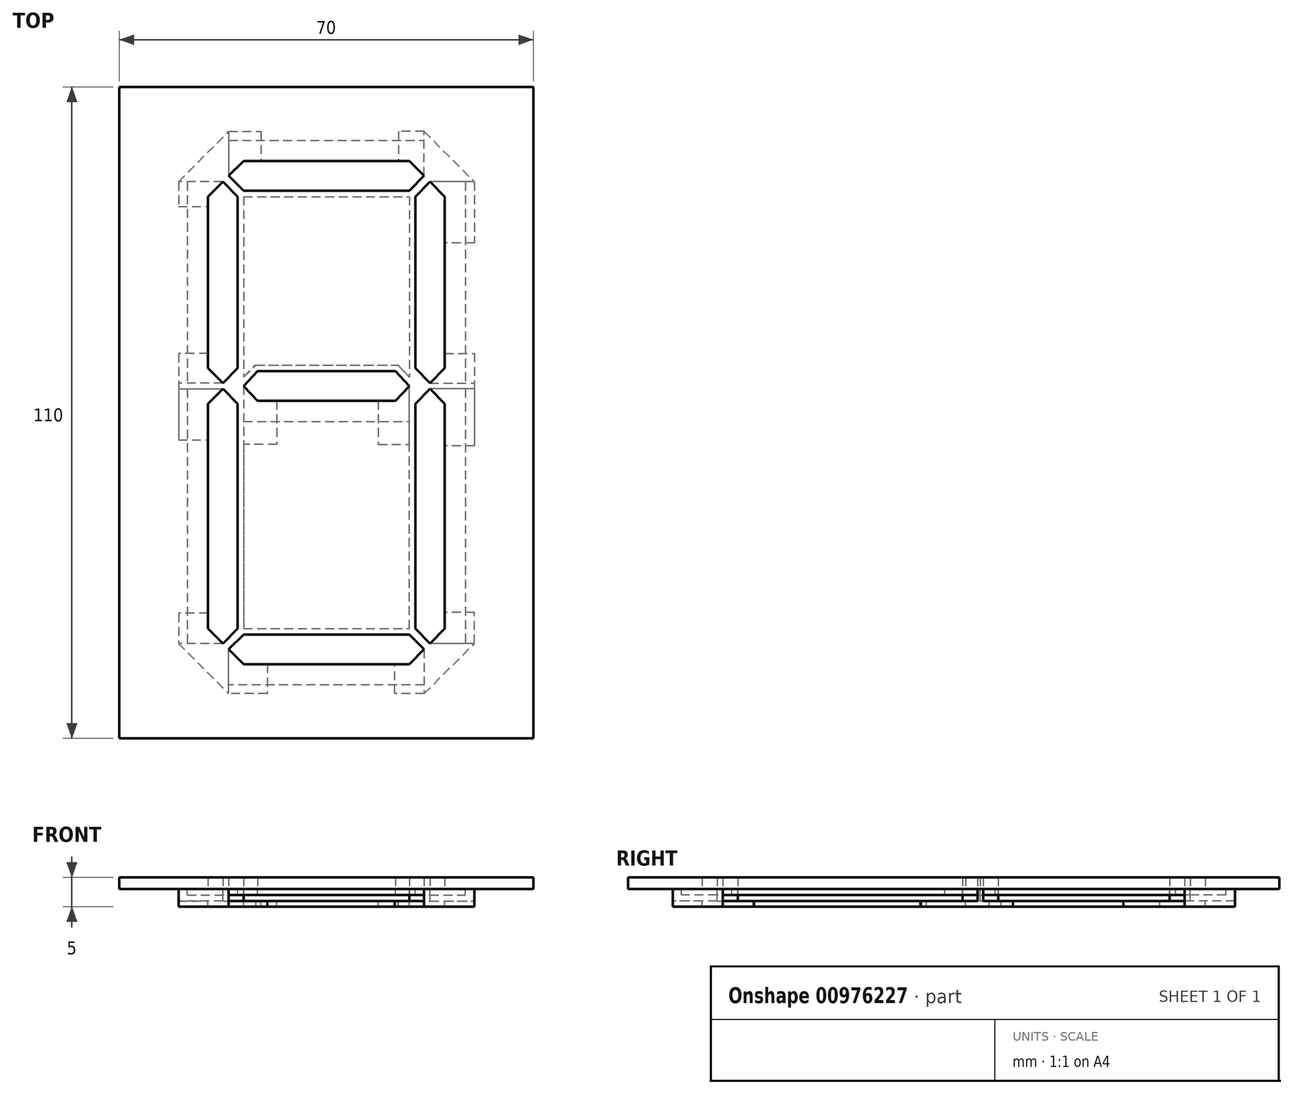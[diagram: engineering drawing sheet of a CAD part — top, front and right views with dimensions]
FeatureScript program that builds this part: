
annotation { "Feature Type Name" : "Feature", "Feature Type Description" : "" }
export const myFeature = defineFeature(function(context is Context, id is Id, definition is map)
    precondition{}
    {
        {
            var Q0;
            Q0=qCreatedBy(makeId("Top.planeOp"),FACE);
            var sketch = newSketch(context, id + "F0", { "sketchPlane" : qUnion([Q0])});
            skLineSegment(sketch, "E0.bottom", {"start": v(0, 0) * mm, "end": v(70, 0) * mm});
            skLineSegment(sketch, "E0.top", {"start": v(0, 110) * mm, "end": v(70, 110) * mm});
            skLineSegment(sketch, "E0.left", {"start": v(0, 0) * mm, "end": v(0, 110) * mm});
            skLineSegment(sketch, "E0.right", {"start": v(70, 0) * mm, "end": v(70, 110) * mm});
            skLineSegment(sketch, "E1.bottom", {"start": v(17.5, 95) * mm, "end": v(52.5, 95) * mm, "construction": true});
            skLineSegment(sketch, "E1.top", {"start": v(17.5, 15) * mm, "end": v(52.5, 15) * mm, "construction": true});
            skLineSegment(sketch, "E1.left", {"start": v(17.5, 95) * mm, "end": v(17.5, 15) * mm, "construction": true});
            skLineSegment(sketch, "E1.right", {"start": v(52.5, 95) * mm, "end": v(52.5, 15) * mm, "construction": true});
            skLineSegment(sketch, "E2", {"start": v(18.5, 95) * mm, "end": v(21, 97.5) * mm});
            skLineSegment(sketch, "E3", {"start": v(21, 97.5) * mm, "end": v(49, 97.5) * mm});
            skLineSegment(sketch, "E4", {"start": v(49, 97.5) * mm, "end": v(51.5, 95) * mm});
            skLineSegment(sketch, "E5.MirrorCS", {"start": v(18.5, 95) * mm, "end": v(21, 92.5) * mm});
            skLineSegment(sketch, "E6.MirrorCS", {"start": v(21, 92.5) * mm, "end": v(49, 92.5) * mm});
            skLineSegment(sketch, "E7.MirrorCS", {"start": v(49, 92.5) * mm, "end": v(51.5, 95) * mm});
            skLineSegment(sketch, "E8", {"start": v(17.5, 95) * mm, "end": v(36.4, 76.1) * mm, "construction": true});
            skLineSegment(sketch, "E9", {"start": v(17.5, 94) * mm, "end": v(20, 91.5) * mm});
            skLineSegment(sketch, "E10", {"start": v(20, 91.5) * mm, "end": v(20, 62.5) * mm});
            skLineSegment(sketch, "E11", {"start": v(20, 62.5) * mm, "end": v(17.5, 60) * mm});
            skLineSegment(sketch, "E12.MirrorCS", {"start": v(17.5, 94) * mm, "end": v(15, 91.5) * mm});
            skLineSegment(sketch, "E13.MirrorCS", {"start": v(15, 91.5) * mm, "end": v(15, 62.5) * mm});
            skLineSegment(sketch, "E14.MirrorCS", {"start": v(15, 62.5) * mm, "end": v(17.5, 60) * mm});
            skLineSegment(sketch, "E15.MirrorCS", {"start": v(21, 17.5) * mm, "end": v(49, 17.5) * mm});
            skLineSegment(sketch, "E16.MirrorCS", {"start": v(49, 17.5) * mm, "end": v(51.5, 15) * mm});
            skLineSegment(sketch, "E17.MirrorCS", {"start": v(49, 12.5) * mm, "end": v(51.5, 15) * mm});
            skLineSegment(sketch, "E18.MirrorCS", {"start": v(21, 12.5) * mm, "end": v(49, 12.5) * mm});
            skLineSegment(sketch, "E19.MirrorCS", {"start": v(18.5, 15) * mm, "end": v(21, 12.5) * mm});
            skLineSegment(sketch, "E20.MirrorCS", {"start": v(18.5, 15) * mm, "end": v(21, 17.5) * mm});
            skLineSegment(sketch, "E21.MirrorCS", {"start": v(17.5, 16) * mm, "end": v(20, 18.5) * mm});
            skLineSegment(sketch, "E22.MirrorCS", {"start": v(17.5, 16) * mm, "end": v(15, 18.5) * mm});
            skLineSegment(sketch, "E23.MirrorCS", {"start": v(15, 18.5) * mm, "end": v(15, 56.5) * mm});
            skLineSegment(sketch, "E24.MirrorCS", {"start": v(20, 18.5) * mm, "end": v(20, 56.5) * mm});
            skLineSegment(sketch, "E25.MirrorCS", {"start": v(20, 56.5) * mm, "end": v(17.5, 59) * mm});
            skLineSegment(sketch, "E26.MirrorCS", {"start": v(15, 56.5) * mm, "end": v(17.5, 59) * mm});
            skLineSegment(sketch, "E27", {"start": v(35, 92.07) * mm, "end": v(35, 15) * mm, "construction": true});
            skLineSegment(sketch, "E28.MirrorCS", {"start": v(52.5, 94) * mm, "end": v(50, 91.5) * mm});
            skLineSegment(sketch, "E29.MirrorCS", {"start": v(52.5, 94) * mm, "end": v(55, 91.5) * mm});
            skLineSegment(sketch, "E30.MirrorCS", {"start": v(55, 91.5) * mm, "end": v(55, 62.5) * mm});
            skLineSegment(sketch, "E31.MirrorCS", {"start": v(50, 91.5) * mm, "end": v(50, 62.5) * mm});
            skLineSegment(sketch, "E32.MirrorCS", {"start": v(50, 62.5) * mm, "end": v(52.5, 60) * mm});
            skLineSegment(sketch, "E33.MirrorCS", {"start": v(55, 62.5) * mm, "end": v(52.5, 60) * mm});
            skLineSegment(sketch, "E34.MirrorCS", {"start": v(50, 56.5) * mm, "end": v(52.5, 59) * mm});
            skLineSegment(sketch, "E35.MirrorCS", {"start": v(55, 56.5) * mm, "end": v(52.5, 59) * mm});
            skLineSegment(sketch, "E36.MirrorCS", {"start": v(55, 18.5) * mm, "end": v(55, 56.5) * mm});
            skLineSegment(sketch, "E37.MirrorCS", {"start": v(50, 18.5) * mm, "end": v(50, 56.5) * mm});
            skLineSegment(sketch, "E38.MirrorCS", {"start": v(52.5, 16) * mm, "end": v(50, 18.5) * mm});
            skLineSegment(sketch, "E39.MirrorCS", {"start": v(52.5, 16) * mm, "end": v(55, 18.5) * mm});
            skLineSegment(sketch, "E40", {"start": v(21, 59.5) * mm, "end": v(23.33, 62) * mm});
            skLineSegment(sketch, "E41", {"start": v(23.33, 62) * mm, "end": v(46.67, 62) * mm});
            skLineSegment(sketch, "E42", {"start": v(46.67, 62) * mm, "end": v(49, 59.5) * mm});
            skLineSegment(sketch, "E43.MirrorCS", {"start": v(21, 59.5) * mm, "end": v(23.33, 57) * mm});
            skLineSegment(sketch, "E44.MirrorCS", {"start": v(23.33, 57) * mm, "end": v(46.67, 57) * mm});
            skLineSegment(sketch, "E45.MirrorCS", {"start": v(46.67, 57) * mm, "end": v(49, 59.5) * mm});
            skLineSegment(sketch, "E46", {"start": v(52.5, 59.5) * mm, "end": v(15.97, 59.5) * mm, "construction": true});
            skLineSegment(sketch, "E47", {"start": v(52.5, 59) * mm, "end": v(52.5, 60) * mm, "construction": true});
            skSolve(sketch);
        }
        {
            var Q0;
            Q0 = qSketchRegion(id + "F0", true);
            extrude(context, id + "F1", {"entities" : qUnion([Q0]), "depth" : 2 * mm, "offsetDistance" : 25 * mm});
        }
        {
            var Q0;
            Q0=makeQuery(id+"F1.opExtrude","CAP_FACE",FACE,{"disambiguationData":[OSD([sQuery(id+"F0.wireOp",EDGE,"E0.bottom"),sQuery(id+"F0.wireOp",EDGE,"E0.top"),sQuery(id+"F0.wireOp",EDGE,"E0.left"),sQuery(id+"F0.wireOp",EDGE,"E0.right"),sQuery(id+"F0.wireOp",EDGE,"E2"),sQuery(id+"F0.wireOp",EDGE,"E3"),sQuery(id+"F0.wireOp",EDGE,"E4"),sQuery(id+"F0.wireOp",EDGE,"E5.MirrorCS"),sQuery(id+"F0.wireOp",EDGE,"E6.MirrorCS"),sQuery(id+"F0.wireOp",EDGE,"E7.MirrorCS"),sQuery(id+"F0.wireOp",EDGE,"E9"),sQuery(id+"F0.wireOp",EDGE,"E10"),sQuery(id+"F0.wireOp",EDGE,"E11"),sQuery(id+"F0.wireOp",EDGE,"E12.MirrorCS"),sQuery(id+"F0.wireOp",EDGE,"E13.MirrorCS"),sQuery(id+"F0.wireOp",EDGE,"E14.MirrorCS"),sQuery(id+"F0.wireOp",EDGE,"E15.MirrorCS"),sQuery(id+"F0.wireOp",EDGE,"E16.MirrorCS"),sQuery(id+"F0.wireOp",EDGE,"E17.MirrorCS"),sQuery(id+"F0.wireOp",EDGE,"E18.MirrorCS"),sQuery(id+"F0.wireOp",EDGE,"E19.MirrorCS"),sQuery(id+"F0.wireOp",EDGE,"E20.MirrorCS"),sQuery(id+"F0.wireOp",EDGE,"E21.MirrorCS"),sQuery(id+"F0.wireOp",EDGE,"E22.MirrorCS"),sQuery(id+"F0.wireOp",EDGE,"E23.MirrorCS"),sQuery(id+"F0.wireOp",EDGE,"E24.MirrorCS"),sQuery(id+"F0.wireOp",EDGE,"E25.MirrorCS"),sQuery(id+"F0.wireOp",EDGE,"E26.MirrorCS"),sQuery(id+"F0.wireOp",EDGE,"E28.MirrorCS"),sQuery(id+"F0.wireOp",EDGE,"E29.MirrorCS"),sQuery(id+"F0.wireOp",EDGE,"E30.MirrorCS"),sQuery(id+"F0.wireOp",EDGE,"E31.MirrorCS"),sQuery(id+"F0.wireOp",EDGE,"E32.MirrorCS"),sQuery(id+"F0.wireOp",EDGE,"E33.MirrorCS"),sQuery(id+"F0.wireOp",EDGE,"E34.MirrorCS"),sQuery(id+"F0.wireOp",EDGE,"E35.MirrorCS"),sQuery(id+"F0.wireOp",EDGE,"E36.MirrorCS"),sQuery(id+"F0.wireOp",EDGE,"E37.MirrorCS"),sQuery(id+"F0.wireOp",EDGE,"E38.MirrorCS"),sQuery(id+"F0.wireOp",EDGE,"E39.MirrorCS"),sQuery(id+"F0.wireOp",EDGE,"E40"),sQuery(id+"F0.wireOp",EDGE,"E41"),sQuery(id+"F0.wireOp",EDGE,"E42"),sQuery(id+"F0.wireOp",EDGE,"E43.MirrorCS"),sQuery(id+"F0.wireOp",EDGE,"E44.MirrorCS"),sQuery(id+"F0.wireOp",EDGE,"E45.MirrorCS")])],"isStart":true});
            var sketch = newSketch(context, id + "F2", { "sketchPlane" : qUnion([Q0])});
            skLineSegment(sketch, "E48.0", {"start": v(49, -17.5) * mm, "end": v(51.5, -15) * mm});
            skLineSegment(sketch, "E49.0", {"start": v(52.5, -16) * mm, "end": v(50, -18.5) * mm});
            skLineSegment(sketch, "E50.0", {"start": v(50, -18.5) * mm, "end": v(50, -56.5) * mm});
            skLineSegment(sketch, "E51.0", {"start": v(21, -17.5) * mm, "end": v(49, -17.5) * mm});
            skLineSegment(sketch, "E52.0", {"start": v(18.5, -15) * mm, "end": v(21, -17.5) * mm});
            skLineSegment(sketch, "E53.0", {"start": v(17.5, -16) * mm, "end": v(20, -18.5) * mm});
            skLineSegment(sketch, "E54.0", {"start": v(20, -18.5) * mm, "end": v(20, -56.5) * mm});
            skLineSegment(sketch, "E55.0", {"start": v(20, -56.5) * mm, "end": v(17.5, -59) * mm});
            skLineSegment(sketch, "E56.0", {"start": v(50, -56.5) * mm, "end": v(52.5, -59) * mm});
            skLineSegment(sketch, "E57.0", {"start": v(50, -62.5) * mm, "end": v(52.5, -60) * mm});
            skLineSegment(sketch, "E58.0", {"start": v(50, -91.5) * mm, "end": v(50, -62.5) * mm});
            skLineSegment(sketch, "E59.0", {"start": v(20, -62.5) * mm, "end": v(17.5, -60) * mm});
            skLineSegment(sketch, "E60.0", {"start": v(20, -91.5) * mm, "end": v(20, -62.5) * mm});
            skLineSegment(sketch, "E61.0", {"start": v(17.5, -94) * mm, "end": v(20, -91.5) * mm});
            skLineSegment(sketch, "E62.0", {"start": v(21, -92.5) * mm, "end": v(49, -92.5) * mm});
            skLineSegment(sketch, "E63.0", {"start": v(18.5, -95) * mm, "end": v(21, -92.5) * mm});
            skLineSegment(sketch, "E64.0", {"start": v(52.5, -94) * mm, "end": v(50, -91.5) * mm});
            skLineSegment(sketch, "E65.0", {"start": v(49, -92.5) * mm, "end": v(51.5, -95) * mm});
            skLineSegment(sketch, "E66.0", {"start": v(49, -91.5) * mm, "end": v(49, -61.03) * mm});
            skLineSegment(sketch, "E67.0", {"start": v(21, -91.5) * mm, "end": v(49, -91.5) * mm});
            skLineSegment(sketch, "E68.0", {"start": v(21, -91.5) * mm, "end": v(21, -60.97) * mm});
            skLineSegment(sketch, "E69.0", {"start": v(49, -18.5) * mm, "end": v(49, -51.91) * mm});
            skLineSegment(sketch, "E70.0", {"start": v(21, -18.5) * mm, "end": v(49, -18.5) * mm});
            skLineSegment(sketch, "E71.0", {"start": v(21, -18.5) * mm, "end": v(21, -51.91) * mm});
            skLineSegment(sketch, "E72.0", {"start": v(46.67, -62) * mm, "end": v(49, -59.5) * mm});
            skLineSegment(sketch, "E73.0", {"start": v(23.33, -62) * mm, "end": v(46.67, -62) * mm});
            skLineSegment(sketch, "E74.0", {"start": v(21, -59.5) * mm, "end": v(23.33, -62) * mm});
            skLineSegment(sketch, "E75.0", {"start": v(47.1, -63) * mm, "end": v(48.94, -61.03) * mm});
            skLineSegment(sketch, "E75.1", {"start": v(22.9, -63) * mm, "end": v(47.1, -63) * mm});
            skLineSegment(sketch, "E75.2", {"start": v(21, -60.97) * mm, "end": v(22.9, -63) * mm});
            skLineSegment(sketch, "E76", {"start": v(52.5, -60) * mm, "end": v(60, -60) * mm});
            skLineSegment(sketch, "E77", {"start": v(60, -60) * mm, "end": v(60, -59) * mm});
            skLineSegment(sketch, "E78", {"start": v(60, -59) * mm, "end": v(52.5, -59) * mm});
            skLineSegment(sketch, "E79", {"start": v(17.5, -60) * mm, "end": v(10, -60) * mm});
            skLineSegment(sketch, "E80", {"start": v(10, -60) * mm, "end": v(10, -59) * mm});
            skLineSegment(sketch, "E81", {"start": v(10, -59) * mm, "end": v(17.5, -59) * mm});
            skLineSegment(sketch, "E82", {"start": v(17.5, -94) * mm, "end": v(10, -94) * mm});
            skLineSegment(sketch, "E83", {"start": v(10, -94) * mm, "end": v(18.5, -102.5) * mm});
            skLineSegment(sketch, "E84", {"start": v(18.5, -102.5) * mm, "end": v(18.5, -95) * mm});
            skLineSegment(sketch, "E85", {"start": v(51.5, -95) * mm, "end": v(51.5, -102.5) * mm});
            skLineSegment(sketch, "E86", {"start": v(51.5, -102.5) * mm, "end": v(60, -94) * mm});
            skLineSegment(sketch, "E87", {"start": v(60, -94) * mm, "end": v(52.5, -94) * mm});
            skLineSegment(sketch, "E88", {"start": v(17.5, -16) * mm, "end": v(10, -16) * mm});
            skLineSegment(sketch, "E89", {"start": v(10, -16) * mm, "end": v(18.5, -7.5) * mm});
            skLineSegment(sketch, "E90", {"start": v(18.5, -7.5) * mm, "end": v(18.5, -15) * mm});
            skLineSegment(sketch, "E91", {"start": v(51.5, -15) * mm, "end": v(51.5, -7.5) * mm});
            skLineSegment(sketch, "E92", {"start": v(51.5, -7.5) * mm, "end": v(60, -16) * mm});
            skLineSegment(sketch, "E93", {"start": v(60, -16) * mm, "end": v(52.5, -16) * mm});
            skLineSegment(sketch, "E94", {"start": v(21, -59.5) * mm, "end": v(21, -51.91) * mm});
            skPoint(sketch, "E95.end.orphan", {"position": v(13.46, -52.9) * mm});
            skPoint(sketch, "E95.start.orphan", {"position": v(13.46, -51.84) * mm});
            skLineSegment(sketch, "E96", {"start": v(49, -61.03) * mm, "end": v(48.94, -61.03) * mm});
            skLineSegment(sketch, "E97", {"start": v(49, -59.5) * mm, "end": v(49, -51.91) * mm});
            skSolve(sketch);
        }
        {
            var Q0;
            Q0 = qSketchRegion(id + "F2", true);
            var Q1;
            Q1=makeQuery(id+"F2.imprint","IMPRINT",FACE,{"disambiguationData":[TD([[makeQuery(id+"F2.imprint","IMPRINT",EDGE,{"derivedFrom":sQuery(id+"F2.wireOp",EDGE,"E72.0")}),-1.0]])]});
            extrude(context, id + "F3", {"entities" : qUnion([Q0, Q1]), "operationType" : NewBodyOperationType.ADD, "depth" : 2 * mm, "offsetDistance" : 25 * mm});
        }
        {
            var Q0;
            Q0=makeQuery(id+"F3.opExtrude","CAP_FACE",FACE,{"disambiguationData":[OSD([sQuery(id+"F2.wireOp",EDGE,"E48.0"),sQuery(id+"F2.wireOp",EDGE,"E49.0"),sQuery(id+"F2.wireOp",EDGE,"E50.0"),sQuery(id+"F2.wireOp",EDGE,"E51.0"),sQuery(id+"F2.wireOp",EDGE,"E52.0"),sQuery(id+"F2.wireOp",EDGE,"E53.0"),sQuery(id+"F2.wireOp",EDGE,"E54.0"),sQuery(id+"F2.wireOp",EDGE,"E55.0"),sQuery(id+"F2.wireOp",EDGE,"E56.0"),sQuery(id+"F2.wireOp",EDGE,"E57.0"),sQuery(id+"F2.wireOp",EDGE,"E58.0"),sQuery(id+"F2.wireOp",EDGE,"E59.0"),sQuery(id+"F2.wireOp",EDGE,"E60.0"),sQuery(id+"F2.wireOp",EDGE,"E61.0"),sQuery(id+"F2.wireOp",EDGE,"E62.0"),sQuery(id+"F2.wireOp",EDGE,"E63.0"),sQuery(id+"F2.wireOp",EDGE,"E64.0"),sQuery(id+"F2.wireOp",EDGE,"E65.0"),sQuery(id+"F2.wireOp",EDGE,"E66.0"),sQuery(id+"F2.wireOp",EDGE,"E67.0"),sQuery(id+"F2.wireOp",EDGE,"E68.0"),sQuery(id+"F2.wireOp",EDGE,"E69.0"),sQuery(id+"F2.wireOp",EDGE,"E70.0"),sQuery(id+"F2.wireOp",EDGE,"E71.0"),sQuery(id+"F2.wireOp",EDGE,"84MnlcbP-1qpu-Rj2J-FLr8-rwROh0f0MHm2"),sQuery(id+"F2.wireOp",EDGE,"LZrshJra-HxY4-wUjW-u9oj-DeEecagEfHDl"),sQuery(id+"F2.wireOp",EDGE,"1782aa05-fe14-407d-a0ca-22a35b96d353.0"),sQuery(id+"F2.wireOp",EDGE,"6b285926-bf98-404c-bd19-462a9478543c.0"),sQuery(id+"F2.wireOp",EDGE,"d8a9666b-d601-445d-a0cd-ca6338d9dcee.0"),sQuery(id+"F2.wireOp",EDGE,"e9a28232-7184-4cf5-acbe-2da583ff58bf.0"),sQuery(id+"F2.wireOp",EDGE,"kZ9Jm4wK-r8F3-Mryh-ujSV-tKrf8OWitTA8"),sQuery(id+"F2.wireOp",EDGE,"QViILa1C-kdha-76VF-oS10-NTMmApzbaOET"),sQuery(id+"F2.wireOp",EDGE,"p2RoQ5Td-hEyZ-tQ5M-2kDP-IsppDfMx4xtr"),sQuery(id+"F2.wireOp",EDGE,"9UdBR3Zx-Fciw-YJRm-m8R1-SlRN9uOtdQAB")])],"isStart":false});
            var sketch = newSketch(context, id + "F4", { "sketchPlane" : qUnion([Q0])});
            skLineSegment(sketch, "E98.0", {"start": v(44.1, -91.5) * mm, "end": v(49, -91.5) * mm});
            skLineSegment(sketch, "E99.0", {"start": v(21, -91.5) * mm, "end": v(44.1, -91.5) * mm});
            skLineSegment(sketch, "E100.0", {"start": v(21, -60.97) * mm, "end": v(21, -91.5) * mm});
            skLineSegment(sketch, "E101.0", {"start": v(21, -68.96) * mm, "end": v(21, -60.97) * mm});
            skLineSegment(sketch, "E102.0", {"start": v(21, -18.5) * mm, "end": v(21, -49.63) * mm});
            skLineSegment(sketch, "E103.0", {"start": v(21, -18.5) * mm, "end": v(49, -18.5) * mm});
            skLineSegment(sketch, "E104.0", {"start": v(49, -18.5) * mm, "end": v(49, -18.5) * mm});
            skLineSegment(sketch, "E105.0", {"start": v(49, -18.5) * mm, "end": v(49, -49.63) * mm});
            skLineSegment(sketch, "E106.0", {"start": v(49, -91.5) * mm, "end": v(49, -61.03) * mm});
            skLineSegment(sketch, "E107.0", {"start": v(23.92, -97.5) * mm, "end": v(47.2, -97.5) * mm});
            skLineSegment(sketch, "E108.0", {"start": v(15, -89.86) * mm, "end": v(15, -65) * mm});
            skLineSegment(sketch, "E109.0", {"start": v(15, -21.1) * mm, "end": v(15, -50.37) * mm});
            skLineSegment(sketch, "E110.0", {"start": v(25, -12.5) * mm, "end": v(46.54, -12.5) * mm});
            skLineSegment(sketch, "E111.0", {"start": v(55, -21.25) * mm, "end": v(55, -49.39) * mm});
            skLineSegment(sketch, "E112.0", {"start": v(55, -83.67) * mm, "end": v(55, -65.02) * mm});
            skLineSegment(sketch, "E113.0", {"start": v(23.1, -63) * mm, "end": v(47.1, -63) * mm});
            skLineSegment(sketch, "E114.0", {"start": v(21, -60.97) * mm, "end": v(23.1, -63) * mm});
            skLineSegment(sketch, "E115.0", {"start": v(26.62, -57) * mm, "end": v(43.76, -57) * mm});
            skLineSegment(sketch, "E116.0", {"start": v(49, -61.03) * mm, "end": v(47.1, -63) * mm});
            skLineSegment(sketch, "E117.trimOffspring", {"start": v(21, -60.97) * mm, "end": v(21, -68.96) * mm});
            skPoint(sketch, "E118.orphan", {"position": v(21, -55.59) * mm});
            skLineSegment(sketch, "E119.0", {"start": v(10, -94) * mm, "end": v(18.5, -102.5) * mm});
            skLineSegment(sketch, "E120.0", {"start": v(51.5, -102.5) * mm, "end": v(60, -94) * mm});
            skLineSegment(sketch, "E121", {"start": v(51.5, -102.5) * mm, "end": v(47.2, -102.5) * mm});
            skLineSegment(sketch, "E122", {"start": v(47.2, -102.5) * mm, "end": v(47.2, -97.5) * mm});
            skLineSegment(sketch, "E123", {"start": v(60, -94) * mm, "end": v(60, -83.67) * mm});
            skLineSegment(sketch, "E124", {"start": v(60, -83.67) * mm, "end": v(55, -83.67) * mm});
            skPoint(sketch, "E125.end.orphan", {"position": v(50, -97.5) * mm});
            skPoint(sketch, "E126.orphan", {"position": v(55, -91.5) * mm});
            skPoint(sketch, "E127.orphan", {"position": v(49, -97.5) * mm});
            skLineSegment(sketch, "E128", {"start": v(18.5, -102.5) * mm, "end": v(23.92, -102.5) * mm});
            skLineSegment(sketch, "E129", {"start": v(23.92, -102.5) * mm, "end": v(23.92, -97.5) * mm});
            skLineSegment(sketch, "E130", {"start": v(10, -94) * mm, "end": v(10, -89.86) * mm});
            skLineSegment(sketch, "E131", {"start": v(10, -89.86) * mm, "end": v(15, -89.86) * mm});
            skPoint(sketch, "E132.start.orphan", {"position": v(21, -97.5) * mm});
            skPoint(sketch, "E133.start.orphan", {"position": v(15, -92.5) * mm});
            skPoint(sketch, "E134.orphan", {"position": v(15, -91.5) * mm});
            skLineSegment(sketch, "E135.0", {"start": v(51.5, -7.5) * mm, "end": v(60, -16) * mm});
            skLineSegment(sketch, "E136.0", {"start": v(10, -16) * mm, "end": v(18.5, -7.5) * mm});
            skLineSegment(sketch, "E137", {"start": v(60, -16) * mm, "end": v(60, -21.25) * mm});
            skLineSegment(sketch, "E138", {"start": v(60, -21.25) * mm, "end": v(55, -21.25) * mm});
            skLineSegment(sketch, "E139", {"start": v(51.5, -7.5) * mm, "end": v(46.54, -7.5) * mm});
            skLineSegment(sketch, "E140", {"start": v(46.54, -7.5) * mm, "end": v(46.54, -12.5) * mm});
            skPoint(sketch, "E141.orphan", {"position": v(55, -18.5) * mm});
            skPoint(sketch, "E142.end.orphan", {"position": v(49, -12.5) * mm});
            skPoint(sketch, "E142.start.orphan", {"position": v(50, -12.5) * mm});
            skLineSegment(sketch, "E143", {"start": v(25, -12.5) * mm, "end": v(25, -7.5) * mm});
            skLineSegment(sketch, "E144", {"start": v(25, -7.5) * mm, "end": v(18.5, -7.5) * mm});
            skLineSegment(sketch, "E145", {"start": v(15, -21.1) * mm, "end": v(10, -21.1) * mm});
            skLineSegment(sketch, "E146", {"start": v(10, -21.1) * mm, "end": v(10, -16) * mm});
            skPoint(sketch, "E147.end.orphan", {"position": v(10, -12.5) * mm});
            skPoint(sketch, "E148.orphan", {"position": v(15, -18.5) * mm});
            skPoint(sketch, "E149.orphan", {"position": v(21, -12.5) * mm});
            skLineSegment(sketch, "E150", {"start": v(15, -65) * mm, "end": v(10, -65) * mm});
            skLineSegment(sketch, "E151", {"start": v(10, -65) * mm, "end": v(10, -50.37) * mm});
            skLineSegment(sketch, "E152", {"start": v(10, -50.37) * mm, "end": v(15, -50.37) * mm});
            skPoint(sketch, "E153.start.orphan", {"position": v(15, -62.5) * mm});
            skPoint(sketch, "E154.orphan", {"position": v(15, -56.5) * mm});
            skLineSegment(sketch, "E155", {"start": v(55, -65.02) * mm, "end": v(60, -65.02) * mm});
            skLineSegment(sketch, "E156", {"start": v(60, -65.02) * mm, "end": v(60, -49.39) * mm});
            skLineSegment(sketch, "E157", {"start": v(60, -49.39) * mm, "end": v(55, -49.39) * mm});
            skPoint(sketch, "E158.orphan", {"position": v(55, -62.5) * mm});
            skPoint(sketch, "E159.orphan", {"position": v(55, -56.5) * mm});
            skLineSegment(sketch, "E160", {"start": v(43.76, -57) * mm, "end": v(43.76, -49.63) * mm});
            skLineSegment(sketch, "E161", {"start": v(43.76, -49.63) * mm, "end": v(49, -49.63) * mm});
            skLineSegment(sketch, "E162", {"start": v(26.62, -57) * mm, "end": v(26.62, -49.63) * mm});
            skLineSegment(sketch, "E163", {"start": v(26.62, -49.63) * mm, "end": v(21, -49.63) * mm});
            skPoint(sketch, "E164.0.start.orphan", {"position": v(46.67, -57) * mm});
            skPoint(sketch, "E165.trimOffspring.start.orphan", {"position": v(49, -59.5) * mm});
            skPoint(sketch, "E166.orphan", {"position": v(49, -48.14) * mm});
            skPoint(sketch, "E167.0.start.orphan", {"position": v(21, -59.5) * mm});
            skPoint(sketch, "E168.orphan", {"position": v(23.33, -57) * mm});
            skSolve(sketch);
        }
        {
            var Q0;
            Q0 = qSketchRegion(id + "F4", true);
            var Q1;
            Q1=makeQuery(id+"F4.imprint","IMPRINT",FACE,{"disambiguationData":[TD([[makeQuery(id+"F4.imprint","IMPRINT",EDGE,{"derivedFrom":sQuery(id+"F4.wireOp",EDGE,"807baf41-9f95-4184-b68a-80730ad5c39e.0")}),1.0]])]});
            extrude(context, id + "F5", {"entities" : qUnion([Q0, Q1]), "operationType" : NewBodyOperationType.ADD, "depth" : 1 * mm, "offsetDistance" : 25 * mm});
        }
        {
            var Q0;
            {var subQ0=sQuery(id+"F0.wireOp",EDGE,"E34.MirrorCS");var subQ1=sQuery(id+"F0.wireOp",EDGE,"E33.MirrorCS");var subQ2=sQuery(id+"F0.wireOp",EDGE,"E26.MirrorCS");var subQ3=sQuery(id+"F0.wireOp",EDGE,"E29.MirrorCS");var subQ4=sQuery(id+"F0.wireOp",EDGE,"E39.MirrorCS");var subQ5=sQuery(id+"F0.wireOp",EDGE,"E38.MirrorCS");var subQ6=sQuery(id+"F0.wireOp",EDGE,"E25.MirrorCS");var subQ7=sQuery(id+"F0.wireOp",EDGE,"E36.MirrorCS");var subQ8=sQuery(id+"F0.wireOp",EDGE,"E35.MirrorCS");var subQ9=sQuery(id+"F0.wireOp",EDGE,"E22.MirrorCS");var subQ10=sQuery(id+"F0.wireOp",EDGE,"E21.MirrorCS");var subQ11=sQuery(id+"F0.wireOp",EDGE,"E32.MirrorCS");var subQ12=sQuery(id+"F0.wireOp",EDGE,"E30.MirrorCS");var subQ13=sQuery(id+"F0.wireOp",EDGE,"E18.MirrorCS");var subQ14=sQuery(id+"F0.wireOp",EDGE,"E28.MirrorCS");var subQ15=sQuery(id+"F0.wireOp",EDGE,"E9");var subQ16=sQuery(id+"F0.wireOp",EDGE,"E5.MirrorCS");var subQ17=sQuery(id+"F0.wireOp",EDGE,"E4");var subQ18=sQuery(id+"F0.wireOp",EDGE,"E3");var subQ19=sQuery(id+"F0.wireOp",EDGE,"E2");var subQ20=sQuery(id+"F0.wireOp",EDGE,"E7.MirrorCS");var subQ21=sQuery(id+"F0.wireOp",EDGE,"E0.bottom");var subQ22=sQuery(id+"F0.wireOp",EDGE,"E20.MirrorCS");var subQ23=sQuery(id+"F0.wireOp",EDGE,"E0.right");var subQ24=sQuery(id+"F0.wireOp",EDGE,"E0.top");var subQ25=sQuery(id+"F0.wireOp",EDGE,"E23.MirrorCS");var subQ26=sQuery(id+"F0.wireOp",EDGE,"E0.left");var subQ27=sQuery(id+"F0.wireOp",EDGE,"E11");var subQ28=sQuery(id+"F0.wireOp",EDGE,"E12.MirrorCS");var subQ29=sQuery(id+"F0.wireOp",EDGE,"E13.MirrorCS");var subQ30=sQuery(id+"F0.wireOp",EDGE,"E14.MirrorCS");var subQ31=sQuery(id+"F0.wireOp",EDGE,"E16.MirrorCS");var subQ32=sQuery(id+"F0.wireOp",EDGE,"E17.MirrorCS");var subQ33=sQuery(id+"F0.wireOp",EDGE,"E19.MirrorCS");Q0=makeQuery(id+"F3.boolean.opBoolean","SPLIT",FACE,{"disambiguationData":[TD([makeQuery(id+"F1.opExtrude","SWEPT_FACE",FACE,{"disambiguationData":[OSD([subQ21])]})])],"derivedFrom":makeQuery(id+"F1.opExtrude","CAP_FACE",FACE,{"disambiguationData":[OSD([subQ21,subQ24,subQ26,subQ23,subQ19,subQ18,subQ17,subQ16,sQuery(id+"F0.wireOp",EDGE,"E6.MirrorCS"),subQ20,subQ15,sQuery(id+"F0.wireOp",EDGE,"E10"),subQ27,subQ28,subQ29,subQ30,sQuery(id+"F0.wireOp",EDGE,"E15.MirrorCS"),subQ31,subQ32,subQ13,subQ33,subQ22,subQ10,subQ9,subQ25,sQuery(id+"F0.wireOp",EDGE,"E24.MirrorCS"),subQ6,subQ2,subQ14,subQ3,subQ12,sQuery(id+"F0.wireOp",EDGE,"E31.MirrorCS"),subQ11,subQ1,subQ0,subQ8,subQ7,sQuery(id+"F0.wireOp",EDGE,"E37.MirrorCS"),subQ5,subQ4,sQuery(id+"F0.wireOp",EDGE,"E40"),sQuery(id+"F0.wireOp",EDGE,"E41"),sQuery(id+"F0.wireOp",EDGE,"E42"),sQuery(id+"F0.wireOp",EDGE,"E43.MirrorCS"),sQuery(id+"F0.wireOp",EDGE,"E44.MirrorCS"),sQuery(id+"F0.wireOp",EDGE,"E45.MirrorCS")])],"isStart":true})});}
            var sketch = newSketch(context, id + "F6", { "sketchPlane" : qUnion([Q0])});
            skLineSegment(sketch, "E169.0", {"start": v(21, -92.5) * mm, "end": v(49, -92.5) * mm});
            skLineSegment(sketch, "E170.0", {"start": v(18.5, -95) * mm, "end": v(21, -92.5) * mm});
            skLineSegment(sketch, "E171.0", {"start": v(17.5, -94) * mm, "end": v(20, -91.5) * mm});
            skLineSegment(sketch, "E172.0", {"start": v(20, -91.5) * mm, "end": v(20, -62.5) * mm});
            skLineSegment(sketch, "E173.0", {"start": v(49, -92.5) * mm, "end": v(51.5, -95) * mm});
            skLineSegment(sketch, "E174.0", {"start": v(52.5, -94) * mm, "end": v(50, -91.5) * mm});
            skLineSegment(sketch, "E175.0", {"start": v(50, -91.5) * mm, "end": v(50, -62.5) * mm});
            skLineSegment(sketch, "E176.0", {"start": v(21, -59.5) * mm, "end": v(23.33, -62) * mm});
            skLineSegment(sketch, "E177.0", {"start": v(20, -62.5) * mm, "end": v(17.5, -60) * mm});
            skLineSegment(sketch, "E178.0", {"start": v(23.33, -62) * mm, "end": v(46.67, -62) * mm});
            skLineSegment(sketch, "E179.0", {"start": v(20, -56.5) * mm, "end": v(17.5, -59) * mm});
            skLineSegment(sketch, "E180.0", {"start": v(20, -18.5) * mm, "end": v(20, -56.5) * mm});
            skLineSegment(sketch, "E181.0", {"start": v(50, -62.5) * mm, "end": v(52.5, -60) * mm});
            skLineSegment(sketch, "E182.0", {"start": v(46.67, -62) * mm, "end": v(49, -59.5) * mm});
            skLineSegment(sketch, "E183.0", {"start": v(50, -56.5) * mm, "end": v(52.5, -59) * mm});
            skLineSegment(sketch, "E184.0", {"start": v(50, -18.5) * mm, "end": v(50, -56.5) * mm});
            skLineSegment(sketch, "E185.0", {"start": v(17.5, -16) * mm, "end": v(20, -18.5) * mm});
            skLineSegment(sketch, "E186.0", {"start": v(18.5, -15) * mm, "end": v(21, -17.5) * mm});
            skLineSegment(sketch, "E187.0", {"start": v(21, -17.5) * mm, "end": v(49, -17.5) * mm});
            skLineSegment(sketch, "E188.0", {"start": v(49, -17.5) * mm, "end": v(51.5, -15) * mm});
            skLineSegment(sketch, "E189.0", {"start": v(52.5, -16) * mm, "end": v(50, -18.5) * mm});
            skLineSegment(sketch, "E190", {"start": v(18.5, -95) * mm, "end": v(18.5, -101) * mm});
            skLineSegment(sketch, "E191", {"start": v(18.5, -101) * mm, "end": v(51.5, -101) * mm});
            skLineSegment(sketch, "E192", {"start": v(51.5, -101) * mm, "end": v(51.5, -95) * mm});
            skLineSegment(sketch, "E193", {"start": v(17.5, -94) * mm, "end": v(11.5, -94) * mm});
            skLineSegment(sketch, "E194", {"start": v(11.5, -94) * mm, "end": v(11.5, -60) * mm});
            skLineSegment(sketch, "E195", {"start": v(11.5, -60) * mm, "end": v(17.5, -60) * mm});
            skLineSegment(sketch, "E196", {"start": v(52.5, -94) * mm, "end": v(58.5, -94) * mm});
            skLineSegment(sketch, "E197", {"start": v(58.5, -94) * mm, "end": v(58.5, -60) * mm});
            skLineSegment(sketch, "E198", {"start": v(58.5, -60) * mm, "end": v(52.5, -60) * mm});
            skLineSegment(sketch, "E199", {"start": v(52.5, -59) * mm, "end": v(58.5, -59) * mm});
            skLineSegment(sketch, "E200", {"start": v(58.5, -59) * mm, "end": v(58.5, -16) * mm});
            skLineSegment(sketch, "E201", {"start": v(58.5, -16) * mm, "end": v(52.5, -16) * mm});
            skLineSegment(sketch, "E202", {"start": v(51.5, -15) * mm, "end": v(51.5, -9) * mm});
            skLineSegment(sketch, "E203", {"start": v(51.5, -9) * mm, "end": v(18.5, -9) * mm});
            skLineSegment(sketch, "E204", {"start": v(18.5, -9) * mm, "end": v(18.5, -15) * mm});
            skLineSegment(sketch, "E205", {"start": v(17.5, -59) * mm, "end": v(11.5, -59) * mm});
            skLineSegment(sketch, "E206", {"start": v(11.5, -59) * mm, "end": v(11.5, -16) * mm});
            skLineSegment(sketch, "E207", {"start": v(11.5, -16) * mm, "end": v(17.5, -16) * mm});
            skLineSegment(sketch, "E208", {"start": v(21, -59.5) * mm, "end": v(21, -53.5) * mm});
            skLineSegment(sketch, "E209", {"start": v(21, -53.5) * mm, "end": v(49, -53.5) * mm});
            skLineSegment(sketch, "E210", {"start": v(49, -53.5) * mm, "end": v(49, -59.5) * mm});
            skSolve(sketch);
        }
        {
            var Q0;
            Q0 = qSketchRegion(id + "F6", true);
            extrude(context, id + "F7", {"entities" : qUnion([Q0]), "depth" : 1 * mm, "offsetDistance" : 25 * mm});
        }
    });
